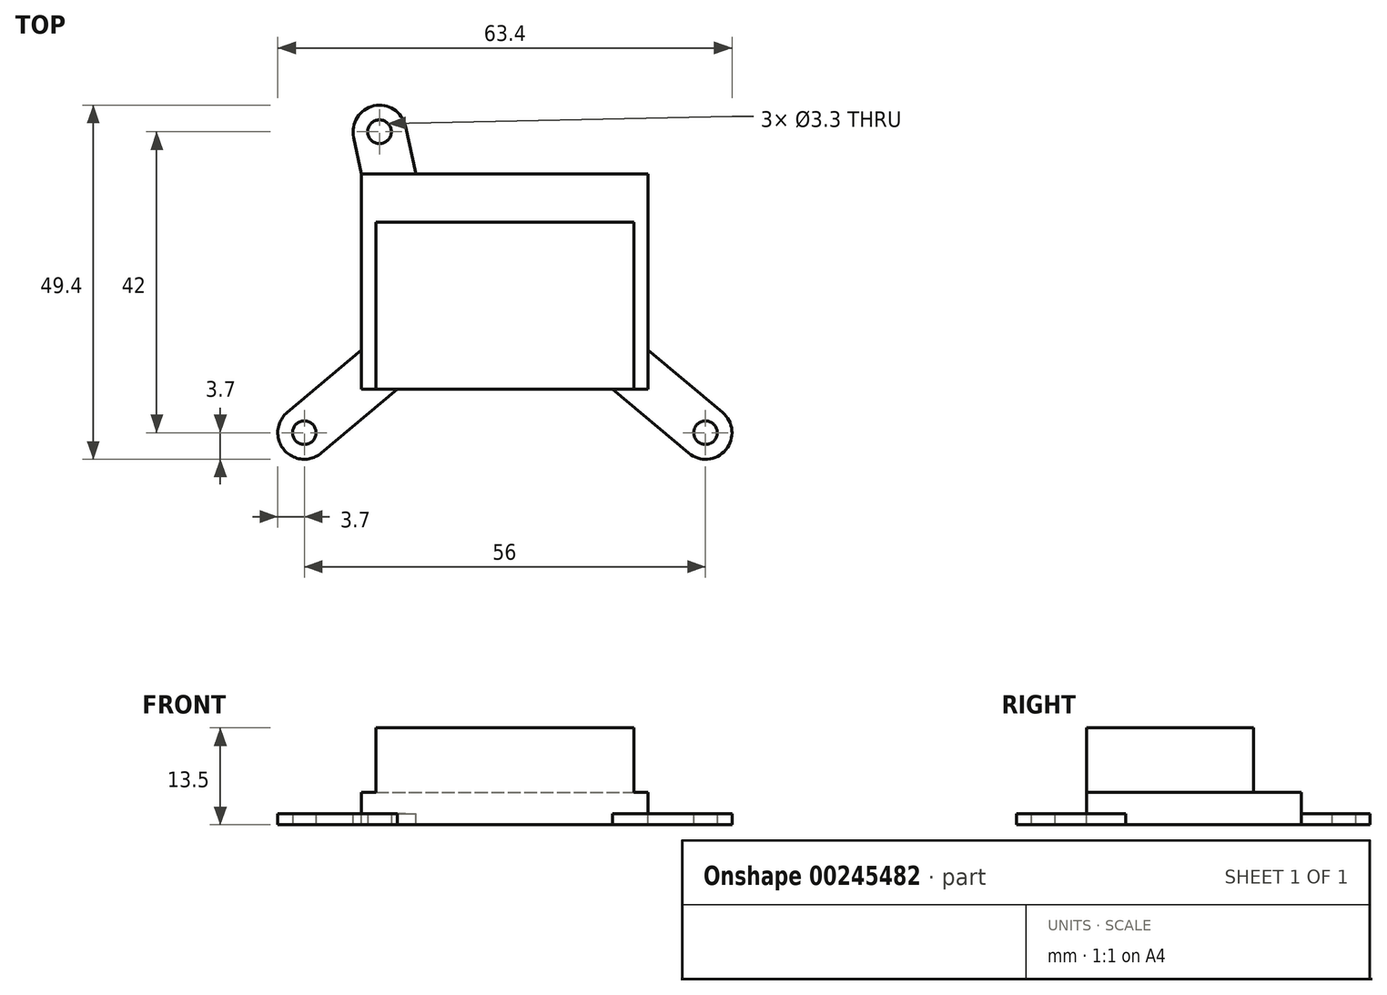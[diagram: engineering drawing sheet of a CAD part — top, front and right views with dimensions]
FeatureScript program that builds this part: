
annotation { "Feature Type Name" : "Feature", "Feature Type Description" : "" }
export const myFeature = defineFeature(function(context is Context, id is Id, definition is map)
    precondition{}
    {
        {
            var Q0;
            Q0=qCreatedBy(makeId("Top.planeOp"),FACE);
            var sketch = newSketch(context, id + "F0", { "sketchPlane" : qUnion([Q0])});
            skLineSegment(sketch, "E0", {"start": v(0, 0) * mm, "end": v(65, 0) * mm});
            skLineSegment(sketch, "E1", {"start": v(32.5, 0) * mm, "end": v(32.5, 107.14) * mm, "construction": true});
            skPoint(sketch, "E2", {"position": v(65.73, 14) * mm});
            skLineSegment(sketch, "E3", {"start": v(65, 0) * mm, "end": v(65.49, 28) * mm, "construction": true});
            skPoint(sketch, "E4.orphan", {"position": v(66.47, 28) * mm});
            skArc(sketch, "E5", {"start": v(65, 0) * mm, "mid": v(65.73, 14) * mm, "end": v(65.49, 28) * mm});
            skLineSegment(sketch, "E6", {"start": v(65.49, 28) * mm, "end": v(57.3, 50.5) * mm});
            skPoint(sketch, "E7", {"position": v(32.5, 63.5) * mm});
            skArc(sketch, "E8.MirrorCS", {"start": v(0, 0) * mm, "mid": v(-0.73, 14) * mm, "end": v(-0.49, 28) * mm});
            skLineSegment(sketch, "E9.MirrorCS", {"start": v(-0.49, 28) * mm, "end": v(7.7, 50.5) * mm});
            skLineSegment(sketch, "E10.MirrorCS", {"start": v(0, 0) * mm, "end": v(-0.49, 28) * mm, "construction": true});
            skPoint(sketch, "E11.MirrorP", {"position": v(-1.47, 28) * mm});
            skPoint(sketch, "E12.MirrorP", {"position": v(-0.73, 14) * mm});
            skArc(sketch, "E13", {"start": v(57.3, 50.5) * mm, "mid": v(32.5, 63.5) * mm, "end": v(7.7, 50.5) * mm});
            skCircle(sketch, "E14", {"center": v(4.5, 12.5) * mm, "radius": 1.65 * mm});
            skCircle(sketch, "E15.MirrorC", {"center": v(60.5, 12.5) * mm, "radius": 1.65 * mm});
            skCircle(sketch, "E16", {"center": v(15, 54.5) * mm, "radius": 1.65 * mm});
            skLineSegment(sketch, "E17", {"start": v(65.73, 14) * mm, "end": v(65.24, 14) * mm});
            skLineSegment(sketch, "E18", {"start": v(-0.73, 14) * mm, "end": v(-0.24, 14) * mm});
            skSolve(sketch);
        }
        {
            var Q0;
            Q0 = qSketchRegion(id + "F0", true);
            extrude(context, id + "F1", {"entities" : qUnion([Q0]), "depth" : 1.5 * mm});
        }
        {
            var Q0;
            Q0=makeQuery(id+"F1.opExtrude","CAP_FACE",FACE,{"disambiguationData":[OSD([sQuery(id+"F0.wireOp",EDGE,"E0"),sQuery(id+"F0.wireOp",EDGE,"E5"),sQuery(id+"F0.wireOp",EDGE,"E6"),sQuery(id+"F0.wireOp",EDGE,"E8.MirrorCS"),sQuery(id+"F0.wireOp",EDGE,"E9.MirrorCS"),sQuery(id+"F0.wireOp",EDGE,"E13"),sQuery(id+"F0.wireOp",EDGE,"E14"),sQuery(id+"F0.wireOp",EDGE,"E15.MirrorC"),sQuery(id+"F0.wireOp",EDGE,"E16")])],"isStart":false});
            var sketch = newSketch(context, id + "F2", { "sketchPlane" : qUnion([Q0])});
            skCircle(sketch, "E19", {"center": v(15, 54.5) * mm, "radius": 3.7 * mm});
            skCircle(sketch, "E20", {"center": v(4.5, 12.5) * mm, "radius": 3.7 * mm});
            skCircle(sketch, "E21", {"center": v(60.5, 12.5) * mm, "radius": 3.7 * mm});
            skLineSegment(sketch, "E22.bottom", {"start": v(12.5, 18.6) * mm, "end": v(52.5, 18.6) * mm});
            skLineSegment(sketch, "E22.top", {"start": v(12.5, 48.6) * mm, "end": v(52.5, 48.6) * mm});
            skLineSegment(sketch, "E22.left", {"start": v(12.5, 18.6) * mm, "end": v(12.5, 48.6) * mm});
            skLineSegment(sketch, "E22.right", {"start": v(52.5, 18.6) * mm, "end": v(52.5, 48.6) * mm});
            skPoint(sketch, "E22.middle", {"position": v(32.5, 33.6) * mm});
            skPoint(sketch, "E22.middle.positionSnap0", {"position": v(32.5, 0) * mm});
            skPoint(sketch, "E22.centerSnap0", {"position": v(32.5, 0) * mm});
            skLineSegment(sketch, "E23", {"start": v(12.5, 48.6) * mm, "end": v(11.39, 53.71) * mm});
            skLineSegment(sketch, "E24", {"start": v(18.61, 55.29) * mm, "end": v(20.07, 48.6) * mm});
            skLineSegment(sketch, "E25", {"start": v(62.88, 15.33) * mm, "end": v(52.5, 24.06) * mm});
            skLineSegment(sketch, "E26", {"start": v(58.12, 9.67) * mm, "end": v(47.5, 18.6) * mm});
            skLineSegment(sketch, "E27", {"start": v(2.12, 15.33) * mm, "end": v(12.5, 24.06) * mm});
            skLineSegment(sketch, "E28", {"start": v(6.88, 9.67) * mm, "end": v(17.5, 18.6) * mm});
            skSolve(sketch);
        }
        {
            var Q0;
            {var subQ1=sQuery(id+"F2.wireOp",EDGE,"E23");Q0=makeQuery(id+"F2.imprint","IMPRINT",FACE,{"disambiguationData":[TD([[makeQuery(id+"F2.imprint","IMPRINT",EDGE,{"derivedFrom":subQ1}),1.0]])]});}
            extrude(context, id + "F3", {"entities" : qUnion([Q0]), "operationType" : NewBodyOperationType.REMOVE, "endBound" : BoundingType.THROUGH_ALL, "oppositeDirection" : true, "depth" : 25 * mm});
        }
        {
            var Q0;
            {var subQ0=sQuery(id+"F2.wireOp",EDGE,"E19");var subQ1=makeQuery(id+"F1.opExtrude","CAP_EDGE",EDGE,{"disambiguationData":[OSD([sQuery(id+"F0.wireOp",EDGE,"E13")])],"isStart":false});var subQ2=makeQuery(id+"F2.imprint","INTERSECT",VERTEX,{"disambiguationData":[OD(0.0)],"derivedFrom":[subQ1,subQ0]});Q0=makeQuery(id+"F2.imprint","IMPRINT",FACE,{"disambiguationData":[TD([[makeQuery(id+"F2.imprint","IMPRINT",EDGE,{"disambiguationData":[TD([[subQ2,-1.0]])],"derivedFrom":subQ0}),1.0]])]});}
            extrude(context, id + "F4", {"entities" : qUnion([Q0]), "operationType" : NewBodyOperationType.ADD, "oppositeDirection" : true, "depth" : 1.5 * mm});
        }
        {
            var Q0;
            {var subQ0=sQuery(id+"F0.wireOp",EDGE,"E13");Q0=makeQuery(id+"F4.boolean.opBoolean","MERGE",FACE,{"derivedFrom":[makeQuery(id+"F1.opExtrude","CAP_FACE",FACE,{"disambiguationData":[OSD([sQuery(id+"F0.wireOp",EDGE,"E0"),sQuery(id+"F0.wireOp",EDGE,"E5"),sQuery(id+"F0.wireOp",EDGE,"E6"),sQuery(id+"F0.wireOp",EDGE,"E8.MirrorCS"),sQuery(id+"F0.wireOp",EDGE,"E9.MirrorCS"),subQ0,sQuery(id+"F0.wireOp",EDGE,"E14"),sQuery(id+"F0.wireOp",EDGE,"E15.MirrorC"),sQuery(id+"F0.wireOp",EDGE,"E16")])],"isStart":false}),makeQuery(id+"F4.opExtrude","CAP_FACE",FACE,{"disambiguationData":[OSD([subQ0,sQuery(id+"F2.wireOp",EDGE,"E19")])],"isStart":true})]});}
            var sketch = newSketch(context, id + "F5", { "sketchPlane" : qUnion([Q0])});
            skLineSegment(sketch, "E29.bottom", {"start": v(12.5, 18.6) * mm, "end": v(52.5, 18.6) * mm});
            skLineSegment(sketch, "E29.top", {"start": v(12.5, 48.6) * mm, "end": v(52.5, 48.6) * mm});
            skLineSegment(sketch, "E29.left", {"start": v(12.5, 18.6) * mm, "end": v(12.5, 48.6) * mm});
            skLineSegment(sketch, "E29.right", {"start": v(52.5, 18.6) * mm, "end": v(52.5, 48.6) * mm});
            skSolve(sketch);
        }
        {
            var Q0;
            Q0 = qSketchRegion(id + "F5", true);
            extrude(context, id + "F6", {"entities" : qUnion([Q0]), "operationType" : NewBodyOperationType.ADD, "depth" : 3 * mm});
        }
        {
            var Q0;
            Q0=makeQuery(id+"F6.opExtrude","CAP_FACE",FACE,{"disambiguationData":[OSD([sQuery(id+"F5.wireOp",EDGE,"E29.bottom"),sQuery(id+"F5.wireOp",EDGE,"E29.top"),sQuery(id+"F5.wireOp",EDGE,"E29.left"),sQuery(id+"F5.wireOp",EDGE,"E29.right")])],"isStart":false});
            var sketch = newSketch(context, id + "F7", { "sketchPlane" : qUnion([Q0])});
            skLineSegment(sketch, "E30.bottom", {"start": v(14.5, 18.6) * mm, "end": v(50.5, 18.6) * mm});
            skLineSegment(sketch, "E30.top", {"start": v(14.5, 41.9) * mm, "end": v(50.5, 41.9) * mm});
            skLineSegment(sketch, "E30.left", {"start": v(14.5, 18.6) * mm, "end": v(14.5, 41.9) * mm});
            skLineSegment(sketch, "E30.right", {"start": v(50.5, 18.6) * mm, "end": v(50.5, 41.9) * mm});
            skSolve(sketch);
        }
        {
            var Q0;
            Q0 = qSketchRegion(id + "F7", true);
            extrude(context, id + "F8", {"entities" : qUnion([Q0]), "operationType" : NewBodyOperationType.ADD, "depth" : 9 * mm});
        }
    });
